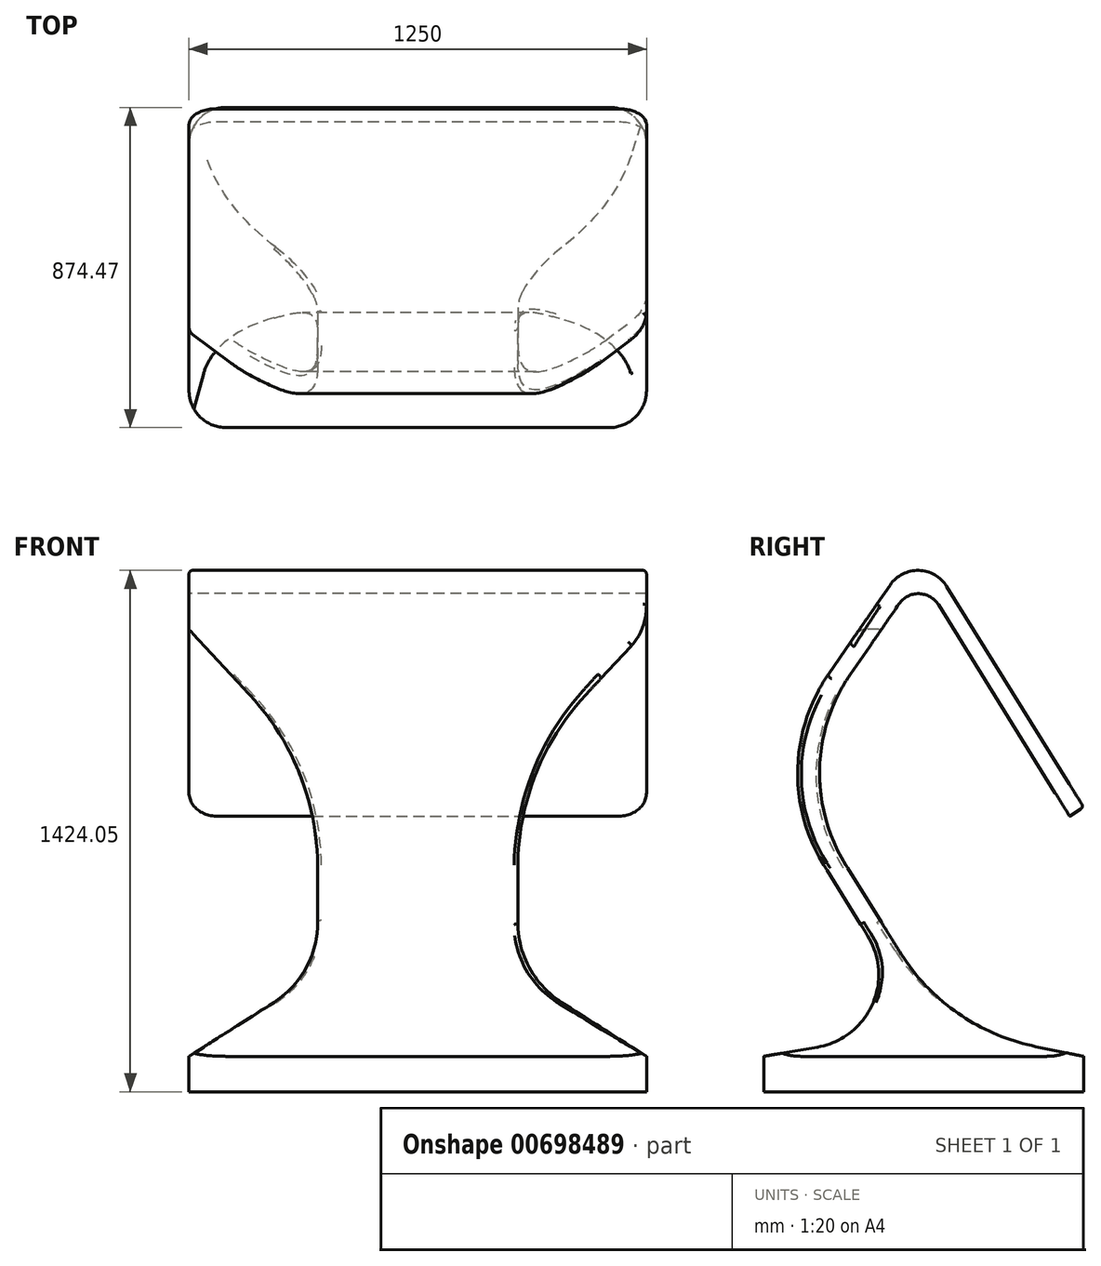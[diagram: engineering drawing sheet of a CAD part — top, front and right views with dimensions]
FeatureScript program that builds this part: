
annotation { "Feature Type Name" : "Feature", "Feature Type Description" : "" }
export const myFeature = defineFeature(function(context is Context, id is Id, definition is map)
    precondition{}
    {
        {
            var Q0;
            Q0=qCreatedBy(makeId("Right.planeOp"),FACE);
            var sketch = newSketch(context, id + "F0", { "sketchPlane" : qUnion([Q0])});
            skLineSegment(sketch, "E0", {"start": v(642.82, -884.41) * mm, "end": v(642.82, -787.78) * mm});
            skLineSegment(sketch, "E1", {"start": v(642.82, -787.78) * mm, "end": v(270.07, -711.85) * mm});
            skLineSegment(sketch, "E2", {"start": v(270.07, -711.85) * mm, "end": v(-171.7, 0) * mm});
            skLineSegment(sketch, "E3", {"start": v(-171.7, 0) * mm, "end": v(194.14, 528.92) * mm});
            skLineSegment(sketch, "E4", {"start": v(194.14, 528.92) * mm, "end": v(603.99, -131.48) * mm});
            skLineSegment(sketch, "E5", {"start": v(603.99, -131.48) * mm, "end": v(642.82, -107.38) * mm});
            skLineSegment(sketch, "E6", {"start": v(642.82, -107.38) * mm, "end": v(194.14, 615.59) * mm});
            skLineSegment(sketch, "E7", {"start": v(194.14, 615.59) * mm, "end": v(-231.65, 0) * mm});
            skLineSegment(sketch, "E8", {"start": v(-231.65, 0) * mm, "end": v(210.13, -711.85) * mm});
            skLineSegment(sketch, "E9", {"start": v(210.13, -711.85) * mm, "end": v(-231.65, -787.78) * mm});
            skLineSegment(sketch, "E10", {"start": v(-231.65, -787.78) * mm, "end": v(-231.65, -884.41) * mm});
            skLineSegment(sketch, "E11", {"start": v(-231.65, -884.41) * mm, "end": v(642.82, -884.41) * mm});
            skSolve(sketch);
        }
        {
            var Q0;
            Q0=makeQuery(id+"F0.imprint","IMPRINT",FACE,{"disambiguationData":[TD([[makeQuery(id+"F0.imprint","IMPRINT",EDGE,{"derivedFrom":sQuery(id+"F0.wireOp",EDGE,"E0")}),1.0]])]});
            extrude(context, id + "F1", {"entities" : qUnion([Q0]), "endBound" : BoundingType.SYMMETRIC, "oppositeDirection" : true, "depth" : 1250 * mm, "offsetDistance" : 25 * mm});
        }
        {
            var Q0;
            Q0=qCreatedBy(makeId("Front.planeOp"),FACE);
            cPlane(context, id + "F2", {"entities" : qUnion([Q0]), "cplaneType" : CPlaneType.OFFSET, "offset" : 652 * mm, "width" : 150 * mm, "height" : 150 * mm});
        }
        {
            var Q0;
            Q0=qCreatedBy(id+"F2.planeOp",FACE);
            var sketch = newSketch(context, id + "F3", { "sketchPlane" : qUnion([Q0])});
            skLineSegment(sketch, "E12", {"start": v(625, 378.4) * mm, "end": v(273.38, 0) * mm});
            skLineSegment(sketch, "E13", {"start": v(273.38, 0) * mm, "end": v(273.38, -564.16) * mm});
            skLineSegment(sketch, "E14.0", {"start": v(-625, -711.85) * mm, "end": v(625, -711.85) * mm, "construction": true});
            skLineSegment(sketch, "E15", {"start": v(273.38, -564.16) * mm, "end": v(625, -711.85) * mm});
            skLineSegment(sketch, "E16", {"start": v(0, 0) * mm, "end": v(0, -354.55) * mm, "construction": true});
            skLineSegment(sketch, "E17.MirrorCS", {"start": v(-625, 378.4) * mm, "end": v(-273.38, 0) * mm});
            skLineSegment(sketch, "E18.MirrorCS", {"start": v(-273.38, 0) * mm, "end": v(-273.38, -564.16) * mm});
            skLineSegment(sketch, "E19.MirrorCS", {"start": v(-273.38, -564.16) * mm, "end": v(-625, -711.85) * mm});
            skLineSegment(sketch, "E20.0", {"start": v(625, 615.59) * mm, "end": v(625, 0) * mm, "construction": true});
            skLineSegment(sketch, "E21", {"start": v(-625, 378.4) * mm, "end": v(-625, -711.85) * mm});
            skLineSegment(sketch, "E22", {"start": v(625, 378.4) * mm, "end": v(625, -711.85) * mm});
            skLineSegment(sketch, "E23.bottom", {"start": v(625, 378.4) * mm, "end": v(1053.94, 378.4) * mm});
            skLineSegment(sketch, "E23.top", {"start": v(625, -711.85) * mm, "end": v(1053.94, -711.85) * mm});
            skLineSegment(sketch, "E23.right", {"start": v(1053.94, 378.4) * mm, "end": v(1053.94, -711.85) * mm});
            skLineSegment(sketch, "E24.bottom", {"start": v(-625, 378.4) * mm, "end": v(-898.27, 378.4) * mm});
            skLineSegment(sketch, "E24.top", {"start": v(-625, -711.85) * mm, "end": v(-898.27, -711.85) * mm});
            skLineSegment(sketch, "E24.right", {"start": v(-898.27, 378.4) * mm, "end": v(-898.27, -711.85) * mm});
            skLineSegment(sketch, "E25.0", {"start": v(-625, -787.78) * mm, "end": v(625, -787.78) * mm, "construction": true});
            skLineSegment(sketch, "E26", {"start": v(273.38, -564.16) * mm, "end": v(625, -787.78) * mm});
            skLineSegment(sketch, "E27", {"start": v(1053.94, -787.78) * mm, "end": v(1053.94, -711.85) * mm});
            skLineSegment(sketch, "E28", {"start": v(625, -787.78) * mm, "end": v(1053.94, -787.78) * mm});
            skLineSegment(sketch, "E29", {"start": v(-273.38, -564.16) * mm, "end": v(-625, -787.78) * mm});
            skLineSegment(sketch, "E30", {"start": v(-898.27, -711.85) * mm, "end": v(-898.27, -787.78) * mm});
            skLineSegment(sketch, "E31", {"start": v(-898.27, -787.78) * mm, "end": v(-625, -787.78) * mm});
            skSolve(sketch);
        }
        {
            var Q0;
            Q0 = qSketchRegion(id + "F3", true);
            extrude(context, id + "F4", {"entities" : qUnion([Q0]), "operationType" : NewBodyOperationType.REMOVE, "oppositeDirection" : true, "depth" : 935 * mm, "offsetDistance" : 25 * mm});
        }
        {
            var Q0;
            {var subQ7=sQuery(id+"F3.wireOp",EDGE,"E29");Q0=makeQuery(id+"F3.imprint","IMPRINT",FACE,{"disambiguationData":[TD([[makeQuery(id+"F3.imprint","IMPRINT",EDGE,{"derivedFrom":subQ7}),-1.0]])]});}
            var Q1;
            {var subQ6=sQuery(id+"F3.wireOp",EDGE,"E26");Q1=makeQuery(id+"F3.imprint","IMPRINT",FACE,{"disambiguationData":[TD([[makeQuery(id+"F3.imprint","IMPRINT",EDGE,{"derivedFrom":subQ6}),1.0]])]});}
            extrude(context, id + "F5", {"entities" : qUnion([Q0, Q1]), "operationType" : NewBodyOperationType.REMOVE, "oppositeDirection" : true, "depth" : 1561 * mm, "offsetDistance" : 25 * mm});
        }
        {
            var Q0;
            Q0=makeQuery(id+"F4.boolean.opBoolean","COPY",EDGE,{"derivedFrom":makeQuery(id+"F4.opExtrude","SWEPT_EDGE",EDGE,{"disambiguationData":[OSD([sQuery(id+"F3.wireOp",EDGE,"E12"),sQuery(id+"F3.wireOp",EDGE,"E13")])]})});
            var Q1;
            Q1=makeQuery(id+"F4.boolean.opBoolean","COPY",EDGE,{"derivedFrom":makeQuery(id+"F4.opExtrude","SWEPT_EDGE",EDGE,{"disambiguationData":[OSD([sQuery(id+"F3.wireOp",EDGE,"E17.MirrorCS"),sQuery(id+"F3.wireOp",EDGE,"E18.MirrorCS")])]})});
            fillet(context, id + "F6", {"entities" : qUnion([Q0, Q1]), "radius" : 695.46 * mm, "tangentPropagation" : true, "allowEdgeOverflow" : false});
        }
        {
            var Q0;
            Q0=makeQuery(id+"F4.boolean.opBoolean","COPY",EDGE,{"derivedFrom":makeQuery(id+"F4.opExtrude","SWEPT_EDGE",EDGE,{"disambiguationData":[OSD([sQuery(id+"F3.wireOp",EDGE,"E18.MirrorCS"),sQuery(id+"F3.wireOp",EDGE,"E19.MirrorCS")])]})});
            var Q1;
            Q1=makeQuery(id+"F4.boolean.opBoolean","COPY",EDGE,{"derivedFrom":makeQuery(id+"F4.opExtrude","SWEPT_EDGE",EDGE,{"disambiguationData":[OSD([sQuery(id+"F3.wireOp",EDGE,"E13"),sQuery(id+"F3.wireOp",EDGE,"E15")])]})});
            fillet(context, id + "F7", {"entities" : qUnion([Q0, Q1]), "radius" : 259.07 * mm, "tangentPropagation" : true, "allowEdgeOverflow" : false});
        }
        {
            var Q0;
            Q0=makeQuery(id+"F1.opExtrude","SWEPT_EDGE",EDGE,{"disambiguationData":[OSD([sQuery(id+"F0.wireOp",EDGE,"E7"),sQuery(id+"F0.wireOp",EDGE,"E8")])]});
            var Q1;
            Q1=makeQuery(id+"F1.opExtrude","SWEPT_EDGE",EDGE,{"disambiguationData":[OSD([sQuery(id+"F0.wireOp",EDGE,"E2"),sQuery(id+"F0.wireOp",EDGE,"E3")])]});
            fillet(context, id + "F8", {"entities" : qUnion([Q0, Q1]), "radius" : 475.15 * mm, "tangentPropagation" : true, "allowEdgeOverflow" : false});
        }
        {
            var Q0;
            {var subQ0=sQuery(id+"F0.wireOp",EDGE,"E8");var subQ1=sQuery(id+"F0.wireOp",EDGE,"E9");Q0=makeQuery(id+"F4.boolean.opBoolean","SPLIT",EDGE,{"disambiguationData":[topologyDisambiguationEdgeConnected([makeQuery(id+"F1.opExtrude","SWEPT_FACE",FACE,{"disambiguationData":[OSD([subQ0])]})])],"derivedFrom":makeQuery(id+"F1.opExtrude","SWEPT_EDGE",EDGE,{"disambiguationData":[OSD([subQ0,subQ1])]})});}
            fillet(context, id + "F9", {"entities" : qUnion([Q0]), "radius" : 201.28 * mm, "tangentPropagation" : true, "allowEdgeOverflow" : false});
        }
        {
            var Q0;
            {var subQ0=sQuery(id+"F0.wireOp",EDGE,"E1");var subQ1=sQuery(id+"F0.wireOp",EDGE,"E2");Q0=makeQuery(id+"F4.boolean.opBoolean","SPLIT",EDGE,{"disambiguationData":[topologyDisambiguationEdgeConnected([makeQuery(id+"F1.opExtrude","SWEPT_FACE",FACE,{"disambiguationData":[OSD([subQ0])]})])],"derivedFrom":makeQuery(id+"F1.opExtrude","SWEPT_EDGE",EDGE,{"disambiguationData":[OSD([subQ0,subQ1])]})});}
            fillet(context, id + "F10", {"entities" : qUnion([Q0]), "radius" : 572.7 * mm, "tangentPropagation" : true, "allowEdgeOverflow" : false});
        }
        {
            var Q0;
            Q0=makeQuery(id+"F1.opExtrude","SWEPT_EDGE",EDGE,{"disambiguationData":[OSD([sQuery(id+"F0.wireOp",EDGE,"E3"),sQuery(id+"F0.wireOp",EDGE,"E4")])]});
            fillet(context, id + "F11", {"entities" : qUnion([Q0]), "radius" : 64.32 * mm, "tangentPropagation" : true, "allowEdgeOverflow" : false});
        }
        {
            var Q0;
            Q0=makeQuery(id+"F1.opExtrude","SWEPT_EDGE",EDGE,{"disambiguationData":[OSD([sQuery(id+"F0.wireOp",EDGE,"E6"),sQuery(id+"F0.wireOp",EDGE,"E7")])]});
            fillet(context, id + "F12", {"entities" : qUnion([Q0]), "radius" : 92.24 * mm, "tangentPropagation" : true, "allowEdgeOverflow" : false});
        }
        {
            var Q0;
            Q0=makeQuery(id+"F4.boolean.opBoolean","COPY",EDGE,{"derivedFrom":makeQuery(id+"F4.opExtrude","SWEPT_EDGE",EDGE,{"disambiguationData":[OSD([sQuery(id+"F3.wireOp",EDGE,"E12"),sQuery(id+"F3.wireOp",EDGE,"E23.bottom"),sQuery(id+"F3.wireOp",EDGE,"E22")])]})});
            var Q1;
            Q1=makeQuery(id+"F4.boolean.opBoolean","COPY",EDGE,{"derivedFrom":makeQuery(id+"F4.opExtrude","SWEPT_EDGE",EDGE,{"disambiguationData":[OSD([sQuery(id+"F3.wireOp",EDGE,"E17.MirrorCS"),sQuery(id+"F3.wireOp",EDGE,"E24.bottom"),sQuery(id+"F3.wireOp",EDGE,"E21")])]})});
            fillet(context, id + "F13", {"entities" : qUnion([Q0, Q1]), "radius" : 161.26 * mm, "tangentPropagation" : true, "allowEdgeOverflow" : false});
        }
        {
            var Q0;
            Q0=makeQuery(id+"F1.opExtrude","CAP_EDGE",EDGE,{"disambiguationData":[OSD([sQuery(id+"F0.wireOp",EDGE,"E5")])],"isStart":false});
            var Q1;
            Q1=makeQuery(id+"F1.opExtrude","CAP_EDGE",EDGE,{"disambiguationData":[OSD([sQuery(id+"F0.wireOp",EDGE,"E5")])],"isStart":true});
            fillet(context, id + "F14", {"entities" : qUnion([Q0, Q1]), "radius" : 75 * mm, "tangentPropagation" : true, "allowEdgeOverflow" : false});
        }
        {
            var Q0;
            Q0=makeQuery(id+"F1.opExtrude","CAP_EDGE",EDGE,{"disambiguationData":[OSD([sQuery(id+"F0.wireOp",EDGE,"E0")])],"isStart":true});
            var Q1;
            Q1=makeQuery(id+"F1.opExtrude","CAP_EDGE",EDGE,{"disambiguationData":[OSD([sQuery(id+"F0.wireOp",EDGE,"E10")])],"isStart":true});
            var Q2;
            Q2=makeQuery(id+"F1.opExtrude","CAP_EDGE",EDGE,{"disambiguationData":[OSD([sQuery(id+"F0.wireOp",EDGE,"E0")])],"isStart":false});
            var Q3;
            Q3=makeQuery(id+"F1.opExtrude","CAP_EDGE",EDGE,{"disambiguationData":[OSD([sQuery(id+"F0.wireOp",EDGE,"E10")])],"isStart":false});
            fillet(context, id + "F15", {"entities" : qUnion([Q0, Q1, Q2, Q3]), "radius" : 101.4 * mm, "tangentPropagation" : true, "allowEdgeOverflow" : false});
        }
        {
            var Q0;
            Q0=makeQuery(id+"F5.boolean.opBoolean","INTERSECT",EDGE,{"derivedFrom":[makeQuery(id+"F1.opExtrude","SWEPT_FACE",FACE,{"disambiguationData":[OSD([sQuery(id+"F0.wireOp",EDGE,"E1")])]}),makeQuery(id+"F5.opExtrude","SWEPT_FACE",FACE,{"disambiguationData":[OSD([sQuery(id+"F3.wireOp",EDGE,"E29")])]})]});
            var Q1;
            Q1=makeQuery(id+"F4.boolean.opBoolean","INTERSECT",EDGE,{"derivedFrom":[makeQuery(id+"F1.opExtrude","SWEPT_FACE",FACE,{"disambiguationData":[OSD([sQuery(id+"F0.wireOp",EDGE,"E9")])]}),makeQuery(id+"F4.opExtrude","SWEPT_FACE",FACE,{"disambiguationData":[OSD([sQuery(id+"F3.wireOp",EDGE,"E26")])]})]});
            fillet(context, id + "F16", {"entities" : qUnion([Q0, Q1]), "radius" : 10 * mm, "tangentPropagation" : true, "allowEdgeOverflow" : false});
        }
    });
